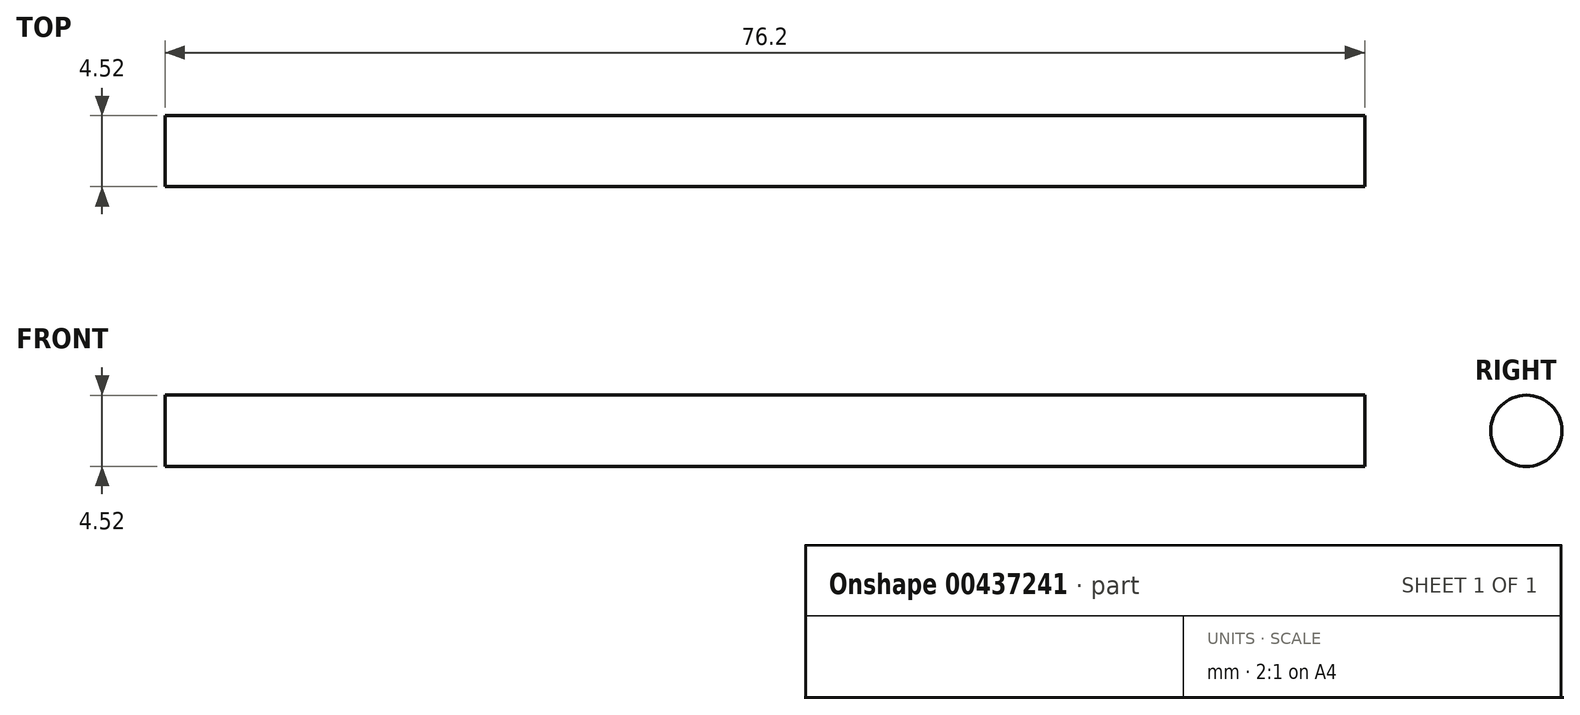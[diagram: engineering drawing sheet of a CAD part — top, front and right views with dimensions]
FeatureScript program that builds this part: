
annotation { "Feature Type Name" : "Feature", "Feature Type Description" : "" }
export const myFeature = defineFeature(function(context is Context, id is Id, definition is map)
    precondition{}
    {
        {
            var Q0;
            Q0=qCreatedBy(makeId("Right.planeOp"),FACE);
            var sketch = newSketch(context, id + "F0", { "sketchPlane" : qUnion([Q0])});
            skCircle(sketch, "E0", {"center": v(0, 0) * mm, "radius": 2.26 * mm});
            skSolve(sketch);
        }
        {
            var Q0;
            Q0 = qSketchRegion(id + "F0", true);
            extrude(context, id + "F1", {"entities" : qUnion([Q0]), "endBound" : BoundingType.SYMMETRIC, "depth" : 76.2 * mm});
        }
    });
